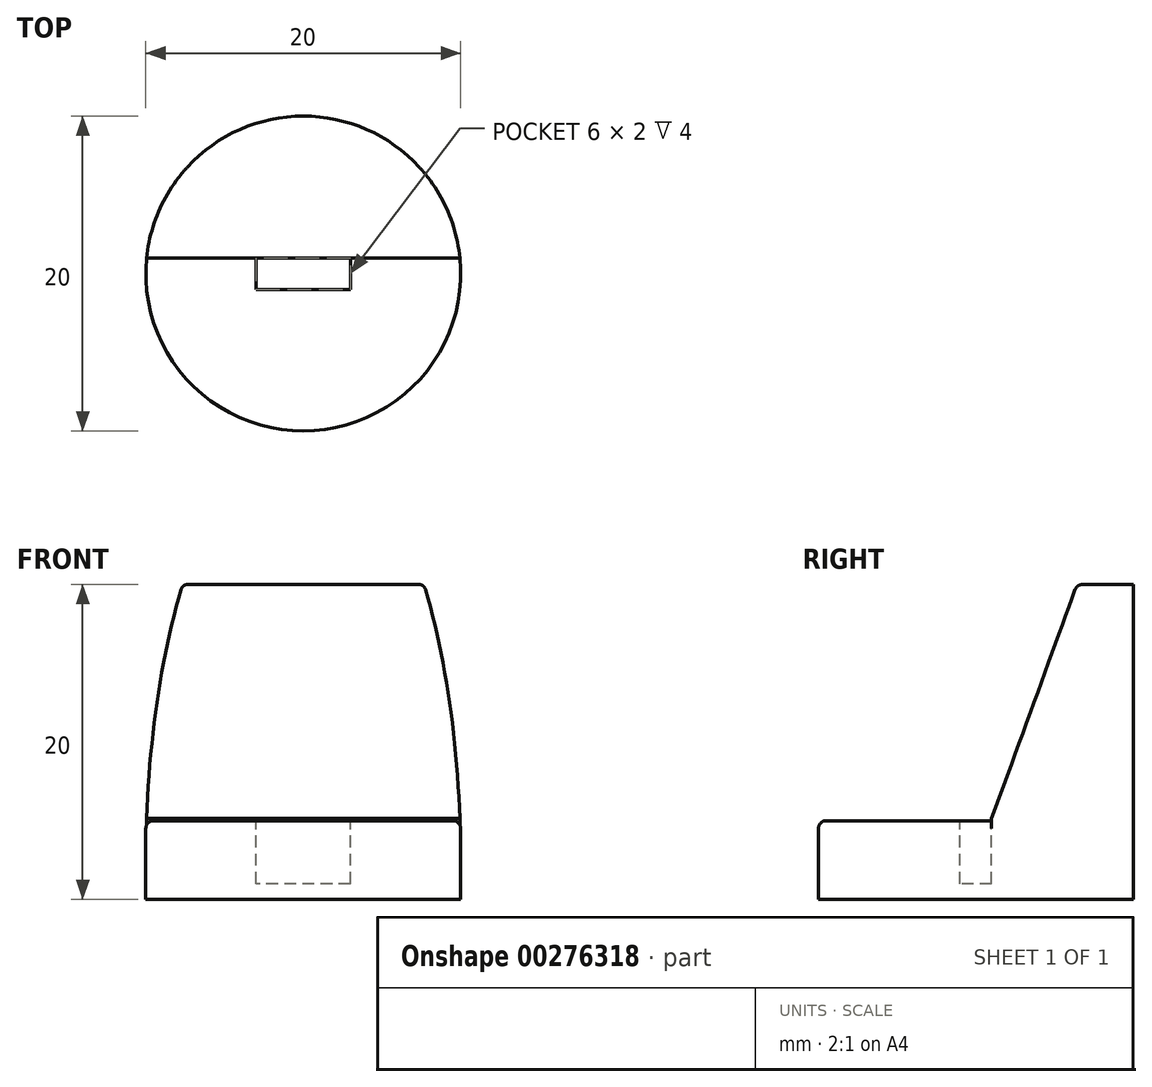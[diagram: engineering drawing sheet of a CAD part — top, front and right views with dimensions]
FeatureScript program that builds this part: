
annotation { "Feature Type Name" : "Feature", "Feature Type Description" : "" }
export const myFeature = defineFeature(function(context is Context, id is Id, definition is map)
    precondition{}
    {
        {
            var Q0;
            Q0=qCreatedBy(makeId("Top.planeOp"),FACE);
            var sketch = newSketch(context, id + "F0", { "sketchPlane" : qUnion([Q0])});
            skCircle(sketch, "E0", {"center": v(0, 0) * mm, "radius": 10 * mm});
            skSolve(sketch);
        }
        {
            var Q0;
            Q0=makeQuery(id+"F0.imprint","IMPRINT",FACE,{"disambiguationData":[TD([[makeQuery(id+"F0.imprint","IMPRINT",EDGE,{"derivedFrom":sQuery(id+"F0.wireOp",EDGE,"E0")}),1.0]])]});
            extrude(context, id + "F1", {"entities" : qUnion([Q0]), "depth" : 5 * mm});
        }
        {
            var Q0;
            Q0=qCreatedBy(makeId("Front.planeOp"),FACE);
            var sketch = newSketch(context, id + "F2", { "sketchPlane" : qUnion([Q0])});
            skLineSegment(sketch, "E1.rect.bottom", {"start": v(3, 1) * mm, "end": v(-3, 1) * mm});
            skLineSegment(sketch, "E1.rect.top", {"start": v(3, 10.8) * mm, "end": v(-3, 10.8) * mm});
            skLineSegment(sketch, "E1.rect.left", {"start": v(3, 1) * mm, "end": v(3, 10.8) * mm});
            skLineSegment(sketch, "E1.rect.right", {"start": v(-3, 1) * mm, "end": v(-3, 10.8) * mm});
            skPoint(sketch, "E1.rect.middle", {"position": v(0, 5.9) * mm});
            skSolve(sketch);
        }
        {
            var Q0;
            Q0=makeQuery(id+"F2.imprint","IMPRINT",FACE,{"disambiguationData":[TD([[makeQuery(id+"F2.imprint","IMPRINT",EDGE,{"derivedFrom":sQuery(id+"F2.wireOp",EDGE,"E1.rect.bottom")}),-1.0]])]});
            extrude(context, id + "F3", {"entities" : qUnion([Q0]), "operationType" : NewBodyOperationType.REMOVE, "endBound" : BoundingType.SYMMETRIC, "oppositeDirection" : true, "depth" : 2 * mm});
        }
        {
            var Q0;
            Q0=makeQuery(id+"F1.opExtrude","CAP_FACE",FACE,{"disambiguationData":[OSD([sQuery(id+"F0.wireOp",EDGE,"E0")])],"isStart":false});
            var sketch = newSketch(context, id + "F4", { "sketchPlane" : qUnion([Q0])});
            skLineSegment(sketch, "E2", {"start": v(-9.95, 1) * mm, "end": v(9.95, 1) * mm});
            skSolve(sketch);
        }
        {
            var Q0;
            {var subQ0=sQuery(id+"F0.wireOp",EDGE,"E0");var subQ1=makeQuery(id+"F1.opExtrude","CAP_EDGE",EDGE,{"disambiguationData":[OSD([subQ0])],"isStart":false});var subQ2=sQuery(id+"F4.wireOp",EDGE,"E2");var subQ4=makeQuery(id+"F4.imprint","INTERSECT",VERTEX,{"disambiguationData":[OD(0.0)],"derivedFrom":[subQ1,subQ2]});Q0=makeQuery(id+"F4.imprint","IMPRINT",FACE,{"disambiguationData":[TD([[makeQuery(id+"F4.imprint","IMPRINT",EDGE,{"disambiguationData":[TD([[subQ4,1.0]])],"derivedFrom":subQ1}),1.0]])]});}
            extrude(context, id + "F5", {"entities" : qUnion([Q0]), "operationType" : NewBodyOperationType.ADD, "depth" : 15 * mm});
        }
        {
            var Q0;
            Q0=qCreatedBy(makeId("Right.planeOp"),FACE);
            var sketch = newSketch(context, id + "F6", { "sketchPlane" : qUnion([Q0])});
            skLineSegment(sketch, "E3", {"start": v(0.97, 5.05) * mm, "end": v(7.15, 22) * mm});
            skLineSegment(sketch, "E4", {"start": v(7.15, 22) * mm, "end": v(0.96, 22) * mm});
            skLineSegment(sketch, "E5", {"start": v(0.96, 22) * mm, "end": v(0.97, 5.05) * mm});
            skSolve(sketch);
        }
        {
            var Q0;
            Q0=qSketchRegion(id+"F6",true);
            extrude(context, id + "F7", {"entities" : qUnion([Q0]), "operationType" : NewBodyOperationType.REMOVE, "endBound" : BoundingType.SYMMETRIC, "oppositeDirection" : true, "depth" : 25 * mm});
        }
        {
            var Q0;
            Q0=makeQuery(id+"F1.opExtrude","CAP_EDGE",EDGE,{"disambiguationData":[OSD([sQuery(id+"F0.wireOp",EDGE,"E0")])],"isStart":false});
            fillet(context, id + "F8", {"entities" : qUnion([Q0]), "radius" : .5 * mm, "tangentPropagation" : true, "allowEdgeOverflow" : false});
        }
        {
            var Q0;
            Q0=makeQuery(id+"F7.boolean.opBoolean","INTERSECT",EDGE,{"derivedFrom":[makeQuery(id+"F5.opExtrude","CAP_FACE",FACE,{"disambiguationData":[OSD([sQuery(id+"F0.wireOp",EDGE,"E0"),sQuery(id+"F4.wireOp",EDGE,"E2")])],"isStart":false}),makeQuery(id+"F7.opExtrude","SWEPT_FACE",FACE,{"disambiguationData":[OSD([sQuery(id+"F6.wireOp",EDGE,"E3")])]})]});
            fillet(context, id + "F9", {"entities" : qUnion([Q0]), "radius" : .5 * mm, "tangentPropagation" : true, "allowEdgeOverflow" : false});
        }
    });
